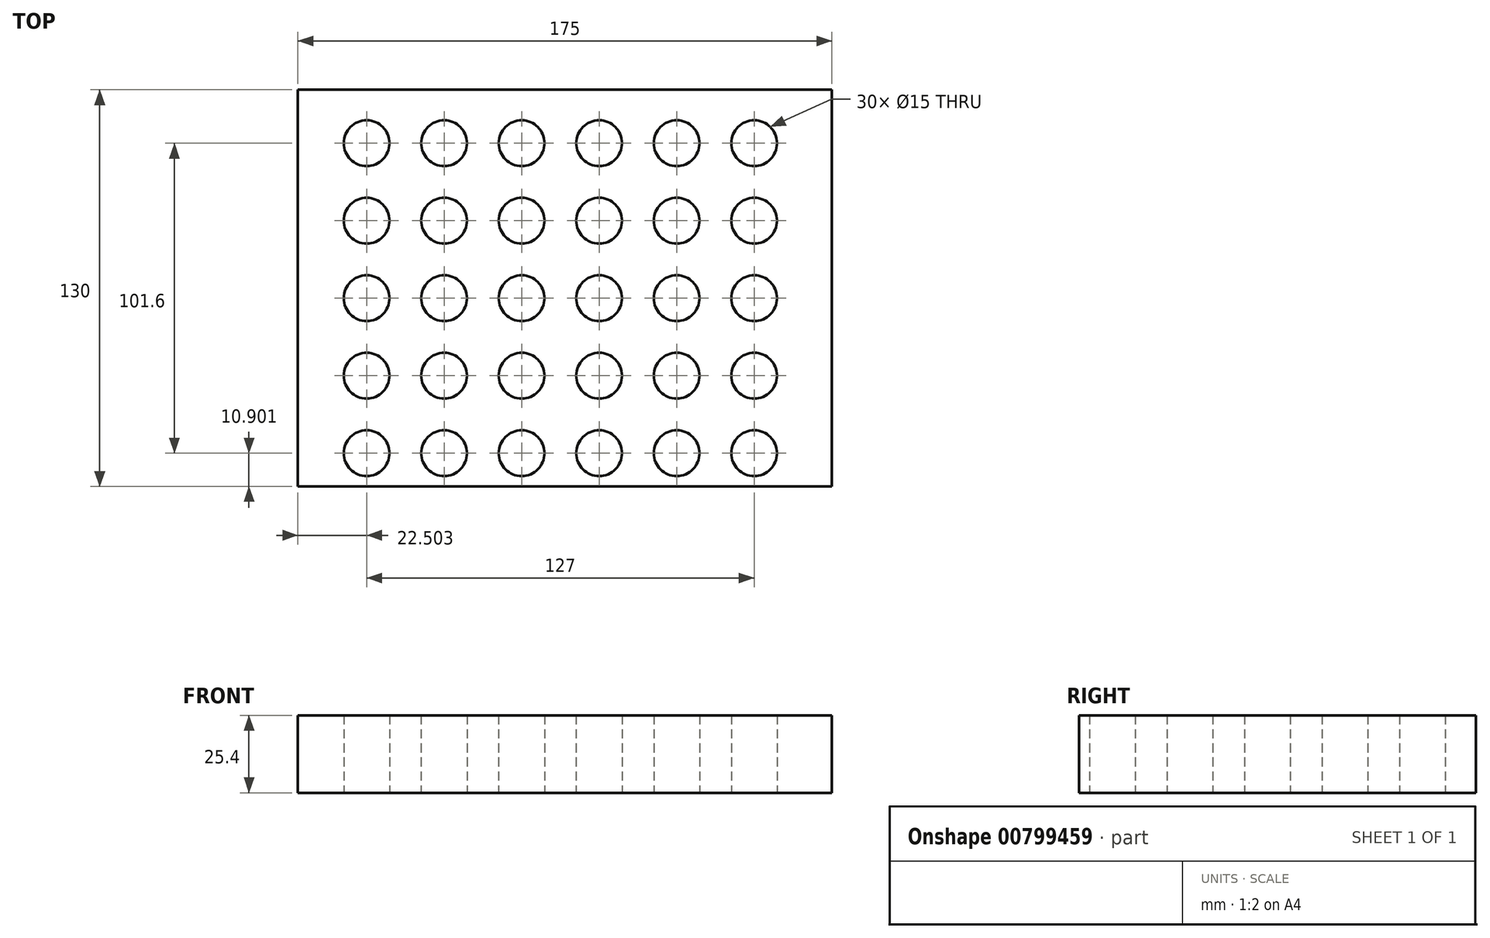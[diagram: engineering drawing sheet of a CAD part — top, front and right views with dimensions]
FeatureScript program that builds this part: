
annotation { "Feature Type Name" : "Feature", "Feature Type Description" : "" }
export const myFeature = defineFeature(function(context is Context, id is Id, definition is map)
    precondition{}
    {
        {
            var Q0;
            Q0=qCreatedBy(makeId("Top.planeOp"),FACE);
            var sketch = newSketch(context, id + "F0", { "sketchPlane" : qUnion([Q0])});
            skLineSegment(sketch, "E0.bottom", {"start": v(-87.6, 65.81) * mm, "end": v(87.4, 65.81) * mm});
            skLineSegment(sketch, "E0.top", {"start": v(-87.6, -64.19) * mm, "end": v(87.4, -64.19) * mm});
            skLineSegment(sketch, "E0.left", {"start": v(-87.6, 65.81) * mm, "end": v(-87.6, -64.19) * mm});
            skLineSegment(sketch, "E0.right", {"start": v(87.4, 65.81) * mm, "end": v(87.4, -64.19) * mm});
            skCircle(sketch, "E1", {"center": v(-65.1, 48.31) * mm, "radius": 7.5 * mm});
            skCircle(sketch, "E2.0.1.0", {"center": v(-65.1, 22.91) * mm, "radius": 7.5 * mm});
            skCircle(sketch, "E2.0.2.0", {"center": v(-65.1, -2.49) * mm, "radius": 7.5 * mm});
            skCircle(sketch, "E2.0.3.0", {"center": v(-65.1, -27.89) * mm, "radius": 7.5 * mm});
            skCircle(sketch, "E2.0.4.0", {"center": v(-65.1, -53.29) * mm, "radius": 7.5 * mm});
            skCircle(sketch, "E2.1.0.0", {"center": v(-39.7, 48.31) * mm, "radius": 7.5 * mm});
            skCircle(sketch, "E2.1.1.0", {"center": v(-39.7, 22.91) * mm, "radius": 7.5 * mm});
            skCircle(sketch, "E2.1.2.0", {"center": v(-39.7, -2.49) * mm, "radius": 7.5 * mm});
            skCircle(sketch, "E2.1.3.0", {"center": v(-39.7, -27.89) * mm, "radius": 7.5 * mm});
            skCircle(sketch, "E2.1.4.0", {"center": v(-39.7, -53.29) * mm, "radius": 7.5 * mm});
            skCircle(sketch, "E2.2.0.0", {"center": v(-14.3, 48.31) * mm, "radius": 7.5 * mm});
            skCircle(sketch, "E2.2.1.0", {"center": v(-14.3, 22.91) * mm, "radius": 7.5 * mm});
            skCircle(sketch, "E2.2.2.0", {"center": v(-14.3, -2.49) * mm, "radius": 7.5 * mm});
            skCircle(sketch, "E2.2.3.0", {"center": v(-14.3, -27.89) * mm, "radius": 7.5 * mm});
            skCircle(sketch, "E2.2.4.0", {"center": v(-14.3, -53.29) * mm, "radius": 7.5 * mm});
            skCircle(sketch, "E2.3.0.0", {"center": v(11.1, 48.31) * mm, "radius": 7.5 * mm});
            skCircle(sketch, "E2.3.1.0", {"center": v(11.1, 22.91) * mm, "radius": 7.5 * mm});
            skCircle(sketch, "E2.3.2.0", {"center": v(11.1, -2.49) * mm, "radius": 7.5 * mm});
            skCircle(sketch, "E2.3.3.0", {"center": v(11.1, -27.89) * mm, "radius": 7.5 * mm});
            skCircle(sketch, "E2.3.4.0", {"center": v(11.1, -53.29) * mm, "radius": 7.5 * mm});
            skCircle(sketch, "E2.4.0.0", {"center": v(36.5, 48.31) * mm, "radius": 7.5 * mm});
            skCircle(sketch, "E2.4.1.0", {"center": v(36.5, 22.91) * mm, "radius": 7.5 * mm});
            skCircle(sketch, "E2.4.2.0", {"center": v(36.5, -2.49) * mm, "radius": 7.5 * mm});
            skCircle(sketch, "E2.4.3.0", {"center": v(36.5, -27.89) * mm, "radius": 7.5 * mm});
            skCircle(sketch, "E2.4.4.0", {"center": v(36.5, -53.29) * mm, "radius": 7.5 * mm});
            skCircle(sketch, "E2.5.0.0", {"center": v(61.9, 48.31) * mm, "radius": 7.5 * mm});
            skCircle(sketch, "E2.5.1.0", {"center": v(61.9, 22.91) * mm, "radius": 7.5 * mm});
            skCircle(sketch, "E2.5.2.0", {"center": v(61.9, -2.49) * mm, "radius": 7.5 * mm});
            skCircle(sketch, "E2.5.3.0", {"center": v(61.9, -27.89) * mm, "radius": 7.5 * mm});
            skCircle(sketch, "E2.5.4.0", {"center": v(61.9, -53.29) * mm, "radius": 7.5 * mm});
            skLineSegment(sketch, "E2.direction1", {"start": v(-65.1, 48.31) * mm, "end": v(-39.7, 48.31) * mm, "construction": true});
            skLineSegment(sketch, "E2.direction2", {"start": v(-65.1, 48.31) * mm, "end": v(-65.1, 22.91) * mm, "construction": true});
            skSolve(sketch);
        }
        {
            var Q0;
            Q0=makeQuery(id+"F0.imprint","IMPRINT",FACE,{"disambiguationData":[TD([[makeQuery(id+"F0.imprint","IMPRINT",EDGE,{"derivedFrom":sQuery(id+"F0.wireOp",EDGE,"E0.bottom")}),-1.0]])]});
            extrude(context, id + "F1", {"entities" : qUnion([Q0]), "depth" : 25.4 * mm, "offsetDistance" : 25.4 * mm});
        }
    });
